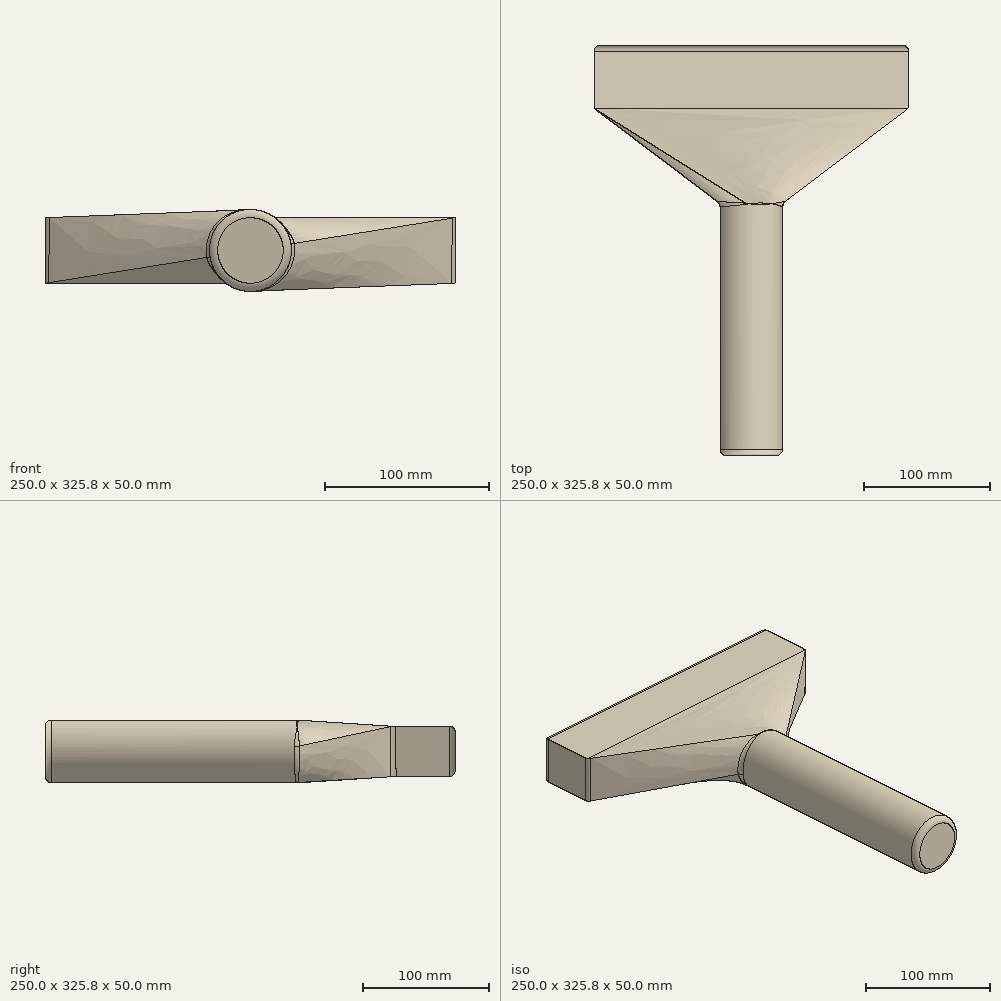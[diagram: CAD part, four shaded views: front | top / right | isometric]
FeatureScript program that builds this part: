
annotation { "Feature Type Name" : "Feature", "Feature Type Description" : "" }
export const myFeature = defineFeature(function(context is Context, id is Id, definition is map)
    precondition{}
    {
        {
            var Q0;
            Q0=qCreatedBy(makeId("Front.planeOp"),FACE);
            var sketch = newSketch(context, id + "F0", { "sketchPlane" : qUnion([Q0])});
            skCircle(sketch, "E0", {"center": v(0, 0) * mm, "radius": 25 * mm});
            skSolve(sketch);
        }
        {
            var Q0;
            Q0=makeQuery(id+"F0.imprint","IMPRINT",FACE,{"disambiguationData":[TD([[makeQuery(id+"F0.imprint","IMPRINT",EDGE,{"derivedFrom":sQuery(id+"F0.wireOp",EDGE,"E0")}),1.0]])]});
            extrude(context, id + "F1", {"entities" : qUnion([Q0]), "depth" : 200 * mm});
        }
        {
            var Q0;
            Q0=qCreatedBy(makeId("Top.planeOp"),FACE);
            var sketch = newSketch(context, id + "F2", { "sketchPlane" : qUnion([Q0])});
            skLineSegment(sketch, "E1.bottom", {"start": v(-125, 125.75) * mm, "end": v(125, 125.75) * mm});
            skLineSegment(sketch, "E1.top", {"start": v(-125, 75.75) * mm, "end": v(125, 75.75) * mm});
            skLineSegment(sketch, "E1.left", {"start": v(-125, 125.75) * mm, "end": v(-125, 75.75) * mm});
            skLineSegment(sketch, "E1.right", {"start": v(125, 125.75) * mm, "end": v(125, 75.75) * mm});
            skSolve(sketch);
        }
        {
            var Q0;
            Q0=makeQuery(id+"F2.imprint","IMPRINT",FACE,{"disambiguationData":[TD([[makeQuery(id+"F2.imprint","IMPRINT",EDGE,{"derivedFrom":sQuery(id+"F2.wireOp",EDGE,"E1.bottom")}),-1.0]])]});
            extrude(context, id + "F3", {"entities" : qUnion([Q0]), "endBound" : BoundingType.SYMMETRIC, "depth" : 40 * mm});
        }
        {
            var Q0;
            Q0=makeQuery(id+"F1.opExtrude","CAP_FACE",FACE,{"disambiguationData":[OSD([sQuery(id+"F0.wireOp",EDGE,"E0")])],"isStart":true});
            var sketch = newSketch(context, id + "F4", { "sketchPlane" : qUnion([Q0])});
            skCircle(sketch, "E2.0", {"center": v(0, 0) * mm, "radius": 25 * mm});
            skLineSegment(sketch, "E3", {"start": v(0, 25) * mm, "end": v(0, -25) * mm, "construction": true});
            skLineSegment(sketch, "E4", {"start": v(-25, 0) * mm, "end": v(25, 0) * mm, "construction": true});
            skLineSegment(sketch, "E5", {"start": v(-17.68, 17.68) * mm, "end": v(-17.68, 17.68) * mm});
            skLineSegment(sketch, "E6", {"start": v(17.68, 17.68) * mm, "end": v(17.68, 17.68) * mm});
            skLineSegment(sketch, "E7", {"start": v(0, 0) * mm, "end": v(17.68, -17.68) * mm, "construction": true});
            skLineSegment(sketch, "E8", {"start": v(0, 0) * mm, "end": v(-17.68, -17.68) * mm, "construction": true});
            skLineSegment(sketch, "E9", {"start": v(17.68, 17.68) * mm, "end": v(0, 0) * mm, "construction": true});
            skLineSegment(sketch, "E10", {"start": v(-17.68, 17.68) * mm, "end": v(0, 0) * mm, "construction": true});
            skLineSegment(sketch, "E11", {"start": v(-17.68, -17.68) * mm, "end": v(-17.68, -17.68) * mm});
            skLineSegment(sketch, "E12", {"start": v(17.68, -17.68) * mm, "end": v(17.68, -17.68) * mm});
            skSolve(sketch);
        }
        {
            var Q1;
            Q1=makeQuery(id+"F4.imprint","IMPRINT",FACE,{"disambiguationData":[TD([[makeQuery(id+"F4.imprint","IMPRINT",EDGE,{"derivedFrom":sQuery(id+"F4.wireOp",EDGE,"E2.0")}),-1.0]])]});
            var Q2;
            Q2=makeQuery(id+"F3.opExtrude","SWEPT_FACE",FACE,{"disambiguationData":[OSD([sQuery(id+"F2.wireOp",EDGE,"E1.top")])]});
            var Q3;
            Q3=sQuery(id+"F4.wireOp",VERTEX,"E3.start");
            var Q4;
            Q4=makeQuery(id+"F3.opExtrude","CAP_VERTEX",VERTEX,{"disambiguationData":[OSD([sQuery(id+"F2.wireOp",EDGE,"E1.top"),sQuery(id+"F2.wireOp",EDGE,"E1.right")])],"isStart":false});
            var Q5;
            Q5=makeQuery(id+"F3.opExtrude","CAP_VERTEX",VERTEX,{"disambiguationData":[OSD([sQuery(id+"F2.wireOp",EDGE,"E1.top"),sQuery(id+"F2.wireOp",EDGE,"E1.left")])],"isStart":false});
            var Q6;
            Q6=sQuery(id+"F4.wireOp",VERTEX,"E4.start");
            var Q7;
            Q7=sQuery(id+"F4.wireOp",VERTEX,"E4.end");
            loft(context, id + "F5", {"operationType" : NewBodyOperationType.ADD, "sheetProfilesArray" : [{ "sheetProfileEntities" : qUnion([Q1]) }, { "sheetProfileEntities" : qUnion([Q2]) }], "connections" : [{ "connectionEntities" : qUnion([Q3, Q4, Q5, Q6, Q7]), "connectionEdgeQueries" : qUnion([]), "connectionEdgeParameters" : [] }]});
        }
        {
            var Q0;
            Q0=makeQuery(id+"F3.opExtrude","SWEPT_EDGE",EDGE,{"disambiguationData":[OSD([sQuery(id+"F2.wireOp",EDGE,"E1.bottom"),sQuery(id+"F2.wireOp",EDGE,"E1.right")])]});
            var Q1;
            Q1=makeQuery(id+"F3.opExtrude","SWEPT_EDGE",EDGE,{"disambiguationData":[OSD([sQuery(id+"F2.wireOp",EDGE,"E1.bottom"),sQuery(id+"F2.wireOp",EDGE,"E1.left")])]});
            var Q2;
            Q2=makeQuery(id+"F3.opExtrude","CAP_EDGE",EDGE,{"disambiguationData":[OSD([sQuery(id+"F2.wireOp",EDGE,"E1.bottom")])],"isStart":true});
            var Q3;
            Q3=makeQuery(id+"F3.opExtrude","CAP_EDGE",EDGE,{"disambiguationData":[OSD([sQuery(id+"F2.wireOp",EDGE,"E1.bottom")])],"isStart":false});
            var Q4;
            {var subQ0=sQuery(id+"F2.wireOp",EDGE,"E1.right");var subQ1=sQuery(id+"F2.wireOp",EDGE,"E1.top");Q4=makeQuery(id+"F5.boolean.opBoolean","MERGE",EDGE,{"derivedFrom":[makeQuery(id+"F3.opExtrude","SWEPT_EDGE",EDGE,{"disambiguationData":[OSD([subQ1,subQ0])]}),makeQuery(id+"F5.opLoft","MID_CAP_EDGE",EDGE,{"disambiguationData":[OSD([subQ1,subQ0])],"capPos":1.0})]});}
            var Q5;
            {var subQ0=sQuery(id+"F4.wireOp",EDGE,"E2.0");var subQ1=sQuery(id+"F2.wireOp",EDGE,"E1.right");var subQ2=sQuery(id+"F2.wireOp",EDGE,"E1.top");var subQ3=sQuery(id+"F2.wireOp",EDGE,"E1.left");Q5=makeQuery(id+"F5.opLoft","MID_CAP_EDGE",EDGE,{"disambiguationData":[OSD([subQ2,subQ3,subQ1,subQ0]),TDD([makeQuery(id+"F3.opExtrude","CAP_VERTEX",VERTEX,{"disambiguationData":[OSD([subQ2,subQ3])],"isStart":false}),makeQuery(id+"F3.opExtrude","CAP_VERTEX",VERTEX,{"disambiguationData":[OSD([subQ2,subQ1])],"isStart":false}),makeQuery(id+"F4.imprint","IMPRINT",EDGE,{"derivedFrom":subQ0})])],"capPos":0.0});}
            var Q6;
            {var subQ0=sQuery(id+"F2.wireOp",EDGE,"E1.left");var subQ1=sQuery(id+"F2.wireOp",EDGE,"E1.top");Q6=makeQuery(id+"F5.boolean.opBoolean","MERGE",EDGE,{"derivedFrom":[makeQuery(id+"F3.opExtrude","SWEPT_EDGE",EDGE,{"disambiguationData":[OSD([subQ1,subQ0])]}),makeQuery(id+"F5.opLoft","MID_CAP_EDGE",EDGE,{"disambiguationData":[OSD([subQ1,subQ0])],"capPos":1.0})]});}
            var Q7;
            {var subQ0=sQuery(id+"F4.wireOp",EDGE,"E2.0");var subQ1=sQuery(id+"F2.wireOp",EDGE,"E1.left");var subQ2=sQuery(id+"F2.wireOp",EDGE,"E1.top");Q7=makeQuery(id+"F5.opLoft","MID_CAP_EDGE",EDGE,{"disambiguationData":[OSD([subQ2,subQ1,subQ0]),TDD([makeQuery(id+"F3.opExtrude","CAP_VERTEX",VERTEX,{"disambiguationData":[OSD([subQ2,subQ1])],"isStart":true}),makeQuery(id+"F4.imprint","IMPRINT",EDGE,{"derivedFrom":subQ0})])],"capPos":0.0});}
            var Q8;
            Q8=makeQuery(id+"F1.opExtrude","CAP_EDGE",EDGE,{"disambiguationData":[OSD([sQuery(id+"F0.wireOp",EDGE,"E0")])],"isStart":false});
            fillet(context, id + "F6", {"entities" : qUnion([Q0, Q1, Q2, Q3, Q4, Q5, Q6, Q7, Q8]), "radius" : 5 * mm, "tangentPropagation" : true, "allowEdgeOverflow" : false});
        }
    });
